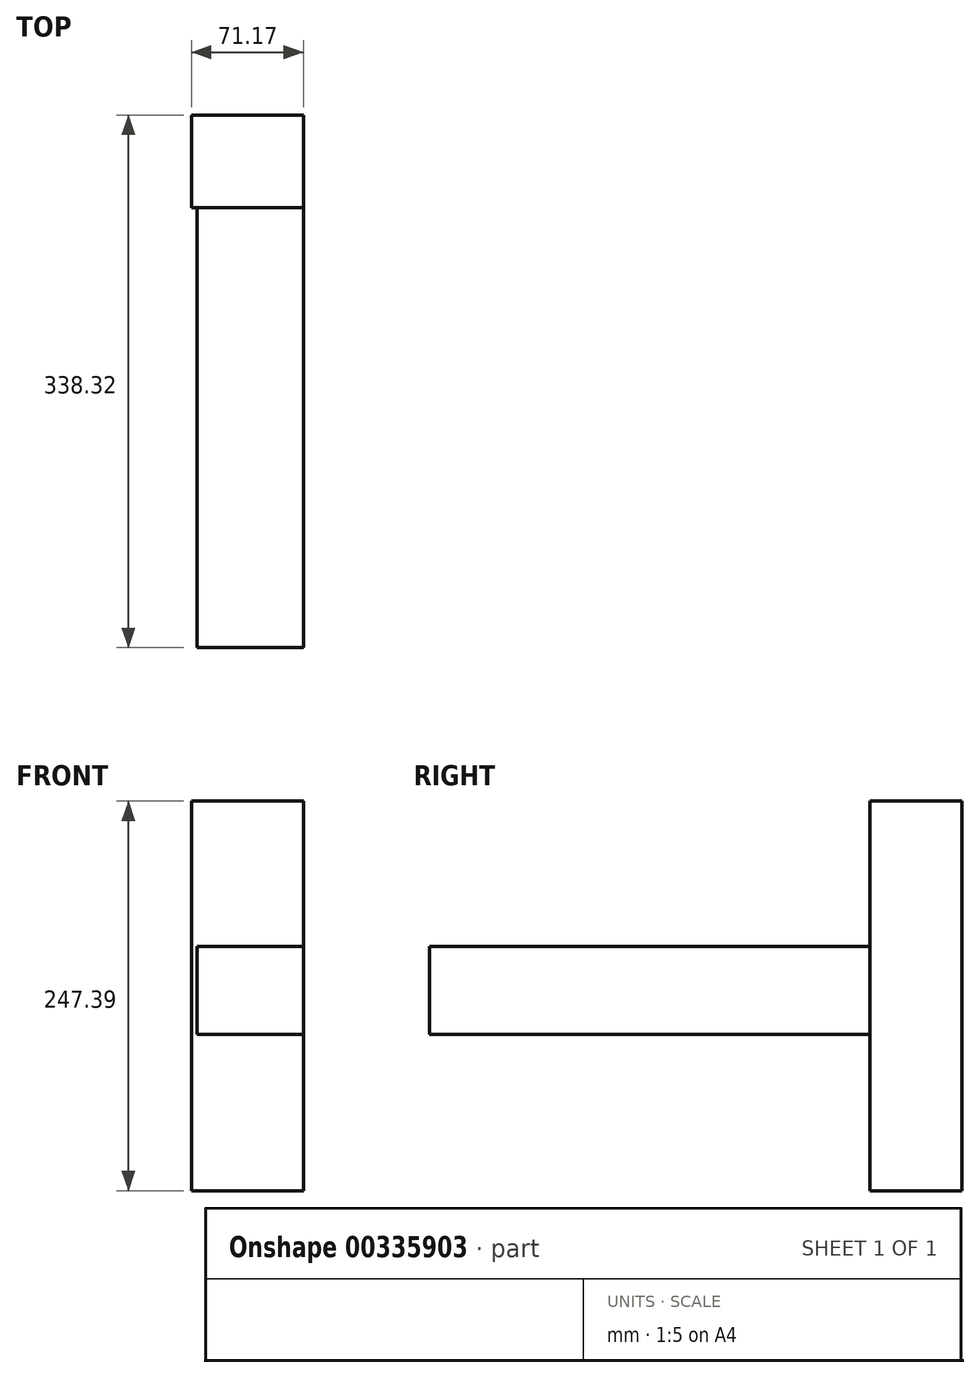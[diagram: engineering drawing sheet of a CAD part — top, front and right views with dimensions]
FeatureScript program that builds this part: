
annotation { "Feature Type Name" : "Feature", "Feature Type Description" : "" }
export const myFeature = defineFeature(function(context is Context, id is Id, definition is map)
    precondition{}
    {
        {
            var Q0;
            Q0=qCreatedBy(makeId("Front.planeOp"),FACE);
            var sketch = newSketch(context, id + "F0", { "sketchPlane" : qUnion([Q0])});
            skLineSegment(sketch, "E0.bottom", {"start": v(0, 0) * mm, "end": v(-67.4, 0) * mm});
            skLineSegment(sketch, "E0.top", {"start": v(0, 55.81) * mm, "end": v(-67.4, 55.81) * mm});
            skLineSegment(sketch, "E0.left", {"start": v(0, 0) * mm, "end": v(0, 55.81) * mm});
            skLineSegment(sketch, "E0.right", {"start": v(-67.4, 0) * mm, "end": v(-67.4, 55.81) * mm});
            skSolve(sketch);
        }
        {
            var Q0;
            Q0=makeQuery(id+"F0.imprint","IMPRINT",FACE,{"disambiguationData":[TD([[makeQuery(id+"F0.imprint","IMPRINT",EDGE,{"derivedFrom":sQuery(id+"F0.wireOp",EDGE,"E0.bottom")}),-1.0]])]});
            extrude(context, id + "F1", {"entities" : qUnion([Q0]), "depth" : 25.4 * mm});
        }
        {
            var Q0;
            Q0=makeQuery(id+"F1.opExtrude","CAP_FACE",FACE,{"disambiguationData":[OSD([sQuery(id+"F0.wireOp",EDGE,"E0.bottom"),sQuery(id+"F0.wireOp",EDGE,"E0.top"),sQuery(id+"F0.wireOp",EDGE,"E0.left"),sQuery(id+"F0.wireOp",EDGE,"E0.right")])],"isStart":false});
            extrude(context, id + "F2", {"entities" : qUnion([Q0]), "operationType" : NewBodyOperationType.ADD, "depth" : 254.25 * mm});
        }
        {
            var Q0;
            Q0=makeQuery(id+"F1.opExtrude","CAP_FACE",FACE,{"disambiguationData":[OSD([sQuery(id+"F0.wireOp",EDGE,"E0.bottom"),sQuery(id+"F0.wireOp",EDGE,"E0.top"),sQuery(id+"F0.wireOp",EDGE,"E0.left"),sQuery(id+"F0.wireOp",EDGE,"E0.right")])],"isStart":true});
            var sketch = newSketch(context, id + "F3", { "sketchPlane" : qUnion([Q0])});
            skLineSegment(sketch, "E1.bottom", {"start": v(71.17, 147.99) * mm, "end": v(0, 147.99) * mm});
            skLineSegment(sketch, "E1.top", {"start": v(71.17, -99.4) * mm, "end": v(0, -99.4) * mm});
            skLineSegment(sketch, "E1.left", {"start": v(71.17, 147.99) * mm, "end": v(71.17, -99.4) * mm});
            skLineSegment(sketch, "E1.right", {"start": v(0, 147.99) * mm, "end": v(0, -99.4) * mm});
            skSolve(sketch);
        }
        {
            var Q0;
            {var subQ2=sQuery(id+"F3.wireOp",EDGE,"E1.bottom");Q0=makeQuery(id+"F3.imprint","IMPRINT",FACE,{"disambiguationData":[TD([[makeQuery(id+"F3.imprint","IMPRINT",EDGE,{"derivedFrom":subQ2}),1.0]])]});}
            var Q1;
            {var subQ1=makeQuery(id+"F1.opExtrude","CAP_EDGE",EDGE,{"disambiguationData":[OSD([sQuery(id+"F0.wireOp",EDGE,"E0.bottom")])],"isStart":true});Q1=makeQuery(id+"F3.imprint","IMPRINT",FACE,{"disambiguationData":[TD([[makeQuery(id+"F3.imprint","IMPRINT",EDGE,{"derivedFrom":subQ1}),1.0]])]});}
            extrude(context, id + "F4", {"entities" : qUnion([Q0, Q1]), "depth" : 58.67 * mm});
        }
    });
